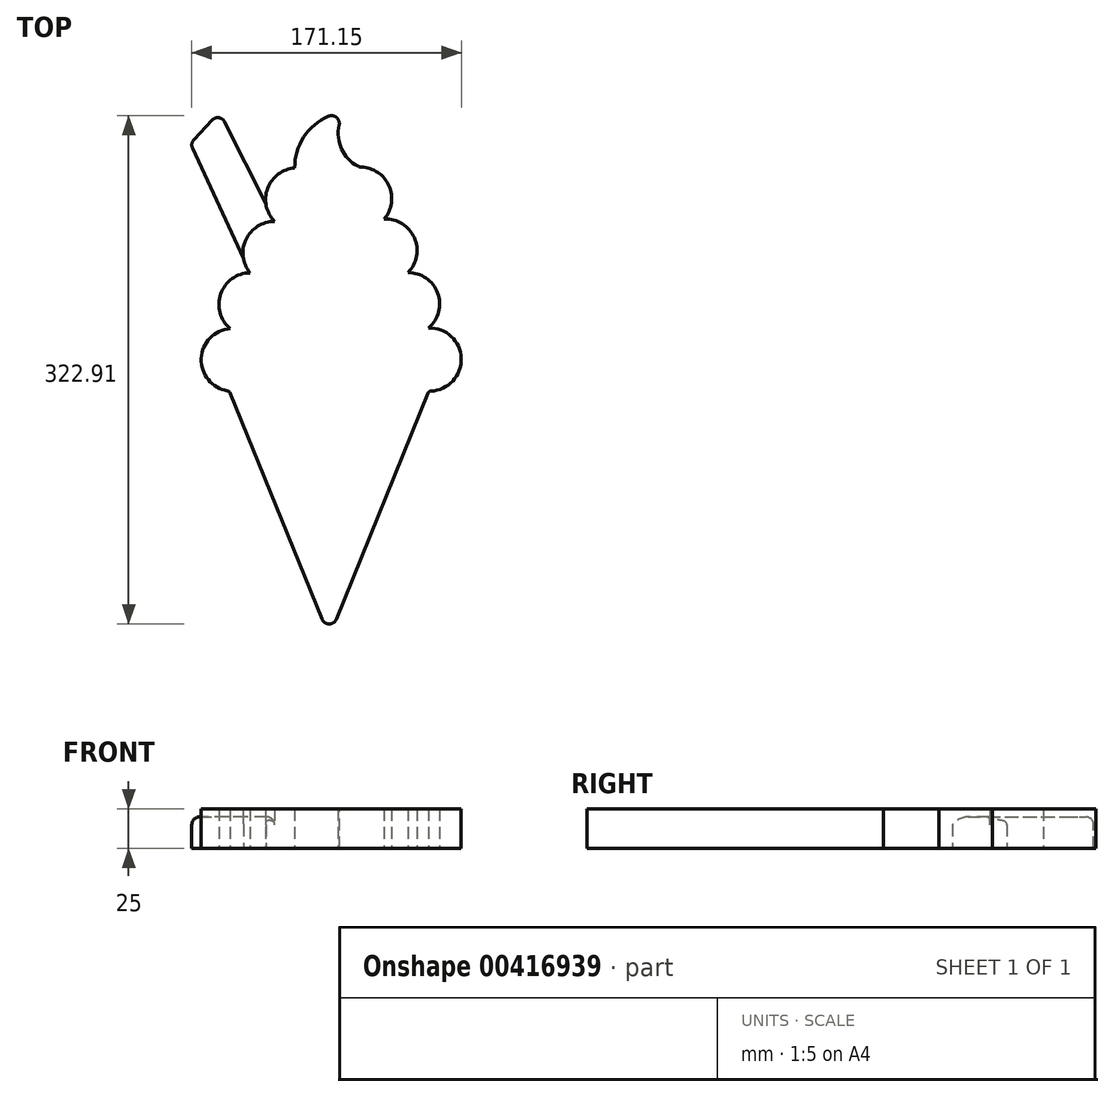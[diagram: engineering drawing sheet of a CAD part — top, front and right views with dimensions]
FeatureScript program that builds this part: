
annotation { "Feature Type Name" : "Feature", "Feature Type Description" : "" }
export const myFeature = defineFeature(function(context is Context, id is Id, definition is map)
    precondition{}
    {
        {
            var Q0;
            Q0=qCreatedBy(makeId("Top.planeOp"),FACE);
            var sketch = newSketch(context, id + "F0", { "sketchPlane" : qUnion([Q0])});
            skLineSegment(sketch, "E0", {"start": v(-63.34, 0) * mm, "end": v(0, -156.22) * mm});
            skLineSegment(sketch, "E1", {"start": v(0, -156.22) * mm, "end": v(63.34, 0) * mm});
            skArc(sketch, "E2", {"start": v(-19.43, 141.74) * mm, "mid": v(-38.63, 129.92) * mm, "end": v(-34.63, 107.73) * mm});
            skArc(sketch, "E3", {"start": v(34.97, 109.34) * mm, "mid": v(37.82, 130.8) * mm, "end": v(19.44, 142.28) * mm});
            skLineSegment(sketch, "E4", {"start": v(-21.88, 141.7) * mm, "end": v(-19.43, 141.74) * mm});
            skArc(sketch, "E5", {"start": v(10.15, 177.38) * mm, "mid": v(-12.77, 165.74) * mm, "end": v(-21.88, 141.7) * mm});
            skArc(sketch, "E6", {"start": v(10.15, 177.38) * mm, "mid": v(6.55, 157.65) * mm, "end": v(19.44, 142.28) * mm});
            skPoint(sketch, "E7.endSnap0", {"position": v(-12.77, 165.74) * mm});
            skPoint(sketch, "E8.endSnap0", {"position": v(6.55, 157.65) * mm});
            skArc(sketch, "E9.trimOffspring", {"start": v(-50.29, 75.1) * mm, "mid": v(-68.9, 61.76) * mm, "end": v(-62.8, 39.69) * mm});
            skArc(sketch, "E10.trimOffspring", {"start": v(-34.63, 107.73) * mm, "mid": v(-52.82, 96.38) * mm, "end": v(-50.29, 75.1) * mm});
            skArc(sketch, "E11.trimOffspring", {"start": v(50.06, 75.33) * mm, "mid": v(54.08, 97.47) * mm, "end": v(34.97, 109.34) * mm});
            skArc(sketch, "E12.trimOffspring", {"start": v(63.18, 40.15) * mm, "mid": v(68.9, 62.32) * mm, "end": v(50.06, 75.33) * mm});
            skLineSegment(sketch, "E13", {"start": v(-34.63, 107.73) * mm, "end": v(-69.5, 177.38) * mm});
            skLineSegment(sketch, "E14", {"start": v(-50.29, 75.1) * mm, "end": v(-88.18, 157.27) * mm});
            skLineSegment(sketch, "E15", {"start": v(-88.18, 157.27) * mm, "end": v(-69.5, 177.38) * mm});
            skArc(sketch, "E16", {"start": v(63.34, 0) * mm, "mid": v(83.9, 20.16) * mm, "end": v(63.18, 40.15) * mm});
            skArc(sketch, "E17", {"start": v(-62.8, 39.69) * mm, "mid": v(-81.24, 20.1) * mm, "end": v(-63.34, 0) * mm});
            skSolve(sketch);
        }
        {
            var Q0;
            {var subQ0=sQuery(id+"F0.wireOp",EDGE,"E4");Q0=makeQuery(id+"F0.imprint","IMPRINT",FACE,{"disambiguationData":[TD([[makeQuery(id+"F0.imprint","IMPRINT",EDGE,{"derivedFrom":subQ0}),1.0]])]});}
            var Q1;
            {var subQ0=sQuery(id+"F0.wireOp",EDGE,"E14");var subQ1=sQuery(id+"F0.wireOp",EDGE,"E10.trimOffspring");var subQ3=makeQuery(id+"F0.imprint","INTERSECT",VERTEX,{"derivedFrom":[subQ1,subQ0]});Q1=makeQuery(id+"F0.imprint","IMPRINT",FACE,{"disambiguationData":[TD([[makeQuery(id+"F0.imprint","IMPRINT",EDGE,{"disambiguationData":[TD([[subQ3,-1.0]])],"derivedFrom":subQ1}),1.0]])]});}
            var Q2;
            {var subQ0=sQuery(id+"F0.wireOp",EDGE,"E13");var subQ1=sQuery(id+"F0.wireOp",EDGE,"E2");var subQ3=makeQuery(id+"F0.imprint","INTERSECT",VERTEX,{"derivedFrom":[subQ1,subQ0]});Q2=makeQuery(id+"F0.imprint","IMPRINT",FACE,{"disambiguationData":[TD([[makeQuery(id+"F0.imprint","IMPRINT",EDGE,{"disambiguationData":[TD([[subQ3,-1.0]])],"derivedFrom":subQ1}),1.0]])]});}
            var Q3;
            {var subQ7=sQuery(id+"F0.wireOp",EDGE,"E1");Q3=makeQuery(id+"F0.imprint","IMPRINT",FACE,{"disambiguationData":[TD([[makeQuery(id+"F0.imprint","IMPRINT",EDGE,{"derivedFrom":subQ7}),1.0]])]});}
            extrude(context, id + "F1", {"entities" : qUnion([Q0, Q1, Q2, Q3]), "depth" : 25 * mm});
        }
        {
            var Q0;
            Q0=makeQuery(id+"F1.opExtrude","SWEPT_EDGE",EDGE,{"disambiguationData":[OSD([sQuery(id+"F0.wireOp",EDGE,"E5"),sQuery(id+"F0.wireOp",EDGE,"E6")])]});
            fillet(context, id + "F2", {"entities" : qUnion([Q0]), "radius" : 5 * mm, "tangentPropagation" : true, "allowEdgeOverflow" : false});
        }
        {
            var Q0;
            Q0=makeQuery(id+"F1.opExtrude","SWEPT_EDGE",EDGE,{"disambiguationData":[OSD([sQuery(id+"F0.wireOp",EDGE,"E0"),sQuery(id+"F0.wireOp",EDGE,"E1")])]});
            fillet(context, id + "F3", {"entities" : qUnion([Q0]), "radius" : 5 * mm, "tangentPropagation" : true, "allowEdgeOverflow" : false});
        }
        {
            var Q0;
            Q0=makeQuery(id+"F1.opExtrude","SWEPT_EDGE",EDGE,{"disambiguationData":[OSD([sQuery(id+"F0.wireOp",EDGE,"E1"),sQuery(id+"F0.wireOp",EDGE,"sioFogSU-8XBV-8isk-VGWu-7kAFjPNIe7ev")])]});
            fillet(context, id + "F4", {"entities" : qUnion([Q0]), "radius" : 2 * mm, "tangentPropagation" : true, "allowEdgeOverflow" : false});
        }
        {
            var Q0;
            Q0=makeQuery(id+"F1.opExtrude","SWEPT_EDGE",EDGE,{"disambiguationData":[OSD([sQuery(id+"F0.wireOp",EDGE,"E0"),sQuery(id+"F0.wireOp",EDGE,"ReNBjHzY-gjhl-lEf1-Hmsf-LibnDAw0oBzZ")])]});
            fillet(context, id + "F5", {"entities" : qUnion([Q0]), "radius" : 2 * mm, "tangentPropagation" : true, "allowEdgeOverflow" : false});
        }
        {
            var Q0;
            Q0=makeQuery(id+"F1.opExtrude","SWEPT_EDGE",EDGE,{"disambiguationData":[OSD([sQuery(id+"F0.wireOp",EDGE,"E3"),sQuery(id+"F0.wireOp",EDGE,"E6")])]});
            fillet(context, id + "F6", {"entities" : qUnion([Q0]), "radius" : 5 * mm, "tangentPropagation" : true, "allowEdgeOverflow" : false});
        }
        {
            var Q0;
            {var subQ0=sQuery(id+"F0.wireOp",EDGE,"E15");Q0=makeQuery(id+"F0.imprint","IMPRINT",FACE,{"disambiguationData":[TD([[makeQuery(id+"F0.imprint","IMPRINT",EDGE,{"derivedFrom":subQ0}),-1.0]])]});}
            extrude(context, id + "F7", {"entities" : qUnion([Q0]), "operationType" : NewBodyOperationType.ADD, "depth" : 20 * mm});
        }
        {
            var Q0;
            Q0=makeQuery(id+"F7.opExtrude","CAP_EDGE",EDGE,{"disambiguationData":[OSD([sQuery(id+"F0.wireOp",EDGE,"E14")])],"isStart":false});
            var Q1;
            Q1=makeQuery(id+"F7.opExtrude","CAP_EDGE",EDGE,{"disambiguationData":[OSD([sQuery(id+"F0.wireOp",EDGE,"E13")])],"isStart":false});
            var Q2;
            Q2=makeQuery(id+"F7.opExtrude","CAP_EDGE",EDGE,{"disambiguationData":[OSD([sQuery(id+"F0.wireOp",EDGE,"E15")])],"isStart":false});
            var Q3;
            Q3=makeQuery(id+"F7.opExtrude","SWEPT_EDGE",EDGE,{"disambiguationData":[OSD([sQuery(id+"F0.wireOp",EDGE,"E14"),sQuery(id+"F0.wireOp",EDGE,"E15")])]});
            var Q4;
            Q4=makeQuery(id+"F7.opExtrude","SWEPT_EDGE",EDGE,{"disambiguationData":[OSD([sQuery(id+"F0.wireOp",EDGE,"E13"),sQuery(id+"F0.wireOp",EDGE,"E15")])]});
            fillet(context, id + "F8", {"entities" : qUnion([Q0, Q1, Q2, Q3, Q4]), "radius" : 5 * mm, "tangentPropagation" : true, "allowEdgeOverflow" : false});
        }
    });
